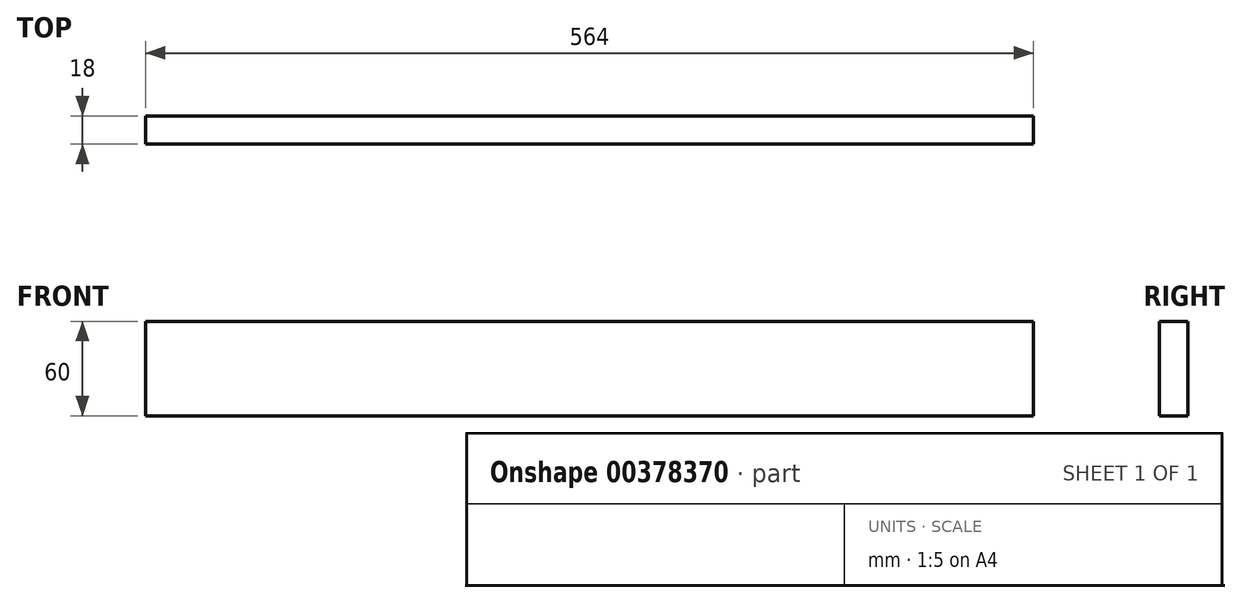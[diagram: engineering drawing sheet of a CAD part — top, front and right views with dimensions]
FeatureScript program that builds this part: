
annotation { "Feature Type Name" : "Feature", "Feature Type Description" : "" }
export const myFeature = defineFeature(function(context is Context, id is Id, definition is map)
    precondition{}
    {
        {
            var Q0;
            Q0=qCreatedBy(makeId("Right.planeOp"),FACE);
            var sketch = newSketch(context, id + "F0", { "sketchPlane" : qUnion([Q0])});
            skLineSegment(sketch, "E0.bottom", {"start": v(9, 30) * mm, "end": v(-9, 30) * mm});
            skLineSegment(sketch, "E0.top", {"start": v(9, -30) * mm, "end": v(-9, -30) * mm});
            skLineSegment(sketch, "E0.left", {"start": v(9, 30) * mm, "end": v(9, -30) * mm});
            skLineSegment(sketch, "E0.right", {"start": v(-9, 30) * mm, "end": v(-9, -30) * mm});
            skPoint(sketch, "E0.middle", {"position": v(0, 0) * mm});
            skSolve(sketch);
        }
        {
            var Q0;
            Q0=qSketchRegion(id+"F0",true);
            extrude(context, id + "F1", {"entities" : qUnion([Q0]), "depth" : 564 * mm});
        }
    });
